# Revit family: Стол кованый «Вена» Арт 6707
name_source: partatom
category: Антураж
revit_build: Autodesk Revit 2018 (Build: 20180423_1000(x64)
units: mm (PartAtom-declared; Revit-internal decimal feet)

## family parameters
Всегда вертикально = Да
Источник визуального образа = Геометрия семейства
На основе рабочей плоскости = Нет
Общий = Нет
При загрузке вырезать с полостями = Нет
Точка расчета площади = Нет

## types (5) — shared parameters
Артикул товара = Арт. 6707
Высота = 760 мм
Группа модели = Садовая и дачная мебель
Изготовитель = ООО «Хоббика»
Изображение типоразмера = Стол кованый «Вена» Арт 6707.jpg
Материал изделия = Сталь, дерево
Цвет опор = Сталь
Цвет столешницы = Дерево
Ширина = 700 мм

## per-type parameters (varying)
| type | Версия 1,2 м | Версия 1,5 м | Версия 1,8 м | Версия 2,0 м | Версия 3,0 м | Длина | Описание |
| Версия 1,2 м | Да | Нет | Нет | Нет | Нет | 1200 мм | Стол кованый «Вена». Версия 1,2 м |
| Версия 1,5 м | Нет | Да | Нет | Нет | Нет | 1500 мм | Стол кованый «Вена». Версия 1,5 м |
| Версия 1,8 м | Нет | Нет | Да | Нет | Нет | 1800 мм | Стол кованый «Вена». Версия 1,8 м |
| Версия 2,0 м | Нет | Нет | Нет | Да | Нет | 2000 мм | Стол кованый «Вена». Версия 2,0 м |
| Версия 3,0 м | Нет | Нет | Нет | Нет | Да | 3000 мм | Стол кованый «Вена». Версия 3,0 м |
